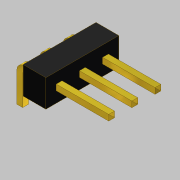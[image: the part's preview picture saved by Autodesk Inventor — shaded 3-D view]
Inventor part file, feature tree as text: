
AUTODESK INVENTOR PART (.ipt)
format: ipt  version: 2012 (Build 160160000, 160)  size: 163,328 bytes
history: native  units: mm (DEFAULTED — no unit token found)
features: sketch x3, sweep x1, plane x1, extrude x1, chamfer x1
ambient origin geometry x8: Origin, YZ Plane, XZ Plane, XY Plane, X Axis, Y Axis, Z Axis, Center Point
bodies: Solid1 (feature_tree)
feature tree (7):
  sweep  "Sweep1"
  plane  "Work Plane1"
  extrude  "Extrusion1"  Depth=4.0mm
  chamfer  "Chamfer1"  Distance=0.5mm
  sketch  "Sketch1"  dims[d0=0.635mm d1=2.54mm]
  sketch  "Sketch2"  dims[d2=2.54mm d3=4.0mm]
  sketch  "Sketch3"  dims[d4=10.0mm d5=0.5mm d6=0.0mm d7=-6.0mm d8=8.0mm d9=3.0mm d10=2.5mm d11=0.0mm d12=0.25mm d13=2.0mm d14=45.0deg]
